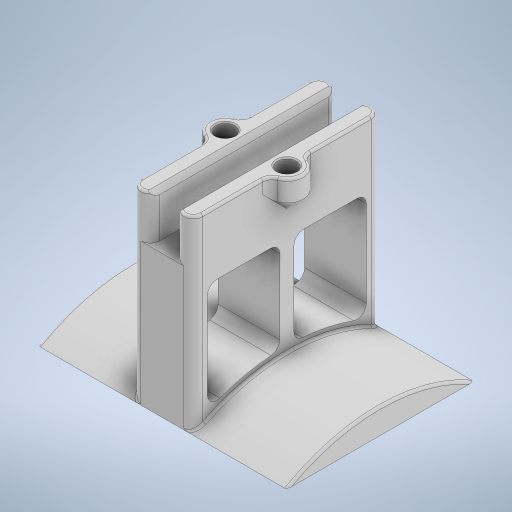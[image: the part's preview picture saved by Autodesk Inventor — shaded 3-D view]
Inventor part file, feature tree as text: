
AUTODESK INVENTOR PART (.ipt)
format: ipt  version: 2023 (Build 270158000, 158)  size: 468,480 bytes
history: native  units: mm
features: extrude x6, sketch x5, fillet x4, chamfer x3, plane x1, mirror x1
ambient origin geometry x8: Origin, YZ Plane, XZ Plane, XY Plane, X Axis, Y Axis, Z Axis, Center Point
bodies: Solid1 (feature_tree)
feature tree (20):
  extrude  "Extrusion1"  Depth=40.0mm
  extrude  "Extrusion2"  Depth=20.0mm TaperAngle=0.0deg
  plane  "Work Plane1"
  mirror  "Mirror1"
  extrude  "Extrusion3"  Depth=5.2mm
  sketch  "Sketch4"  dims[d9=4.0mm d10=9.6mm d11=0.0mm]
  extrude  "Extrusion4"  Depth=9.6mm TaperAngle=0.0deg
  extrude  "Extrusion5"  Depth=2.0mm TaperAngle=45.0deg
  extrude  "Extrusion6"  Depth=1.5mm
  chamfer  "Chamfer2"  Distance=7.0mm
  fillet  "Fillet1"  Radius=8.0mm
  chamfer  "Chamfer1"  Distance=3.1mm
  fillet  "Fillet2"  Radius=2.0mm
  fillet  "Fillet3"  Radius=2.0mm
  chamfer  "Chamfer3"  Distance=0.5mm
  fillet  "Fillet4"  Radius=2.0mm
  sketch  "Sketch1"  dims[d0=40.0mm d1=40.0mm]
  sketch  "Sketch2"  dims[d2=13.2mm d3=0.0mm d5=20.0mm d6=0.0mm]
  sketch  "Sketch3"  dims[d7=-6.6mm d8=5.2mm]
  sketch  "Sketch5"  dims[d12=2.0mm d13=1.0mm d14=2.0mm d15=45.0deg d16=4.1mm d17=7.0mm d18=8.0mm d19=0.0mm d20=3.1mm d21=0.0mm d22=3.5mm d23=2.0mm d24=45.0deg d25=2.0mm d26=0.5mm d27=0.25mm d28=2.0mm d29=45.0deg d30=40.0mm d31=3.0mm d32=3.0mm d33=4.0mm d34=3.0mm d35=42.0mm d36=3.1mm d37=0.0mm d38=2.0mm d39=3.0mm d40=1.5mm]
